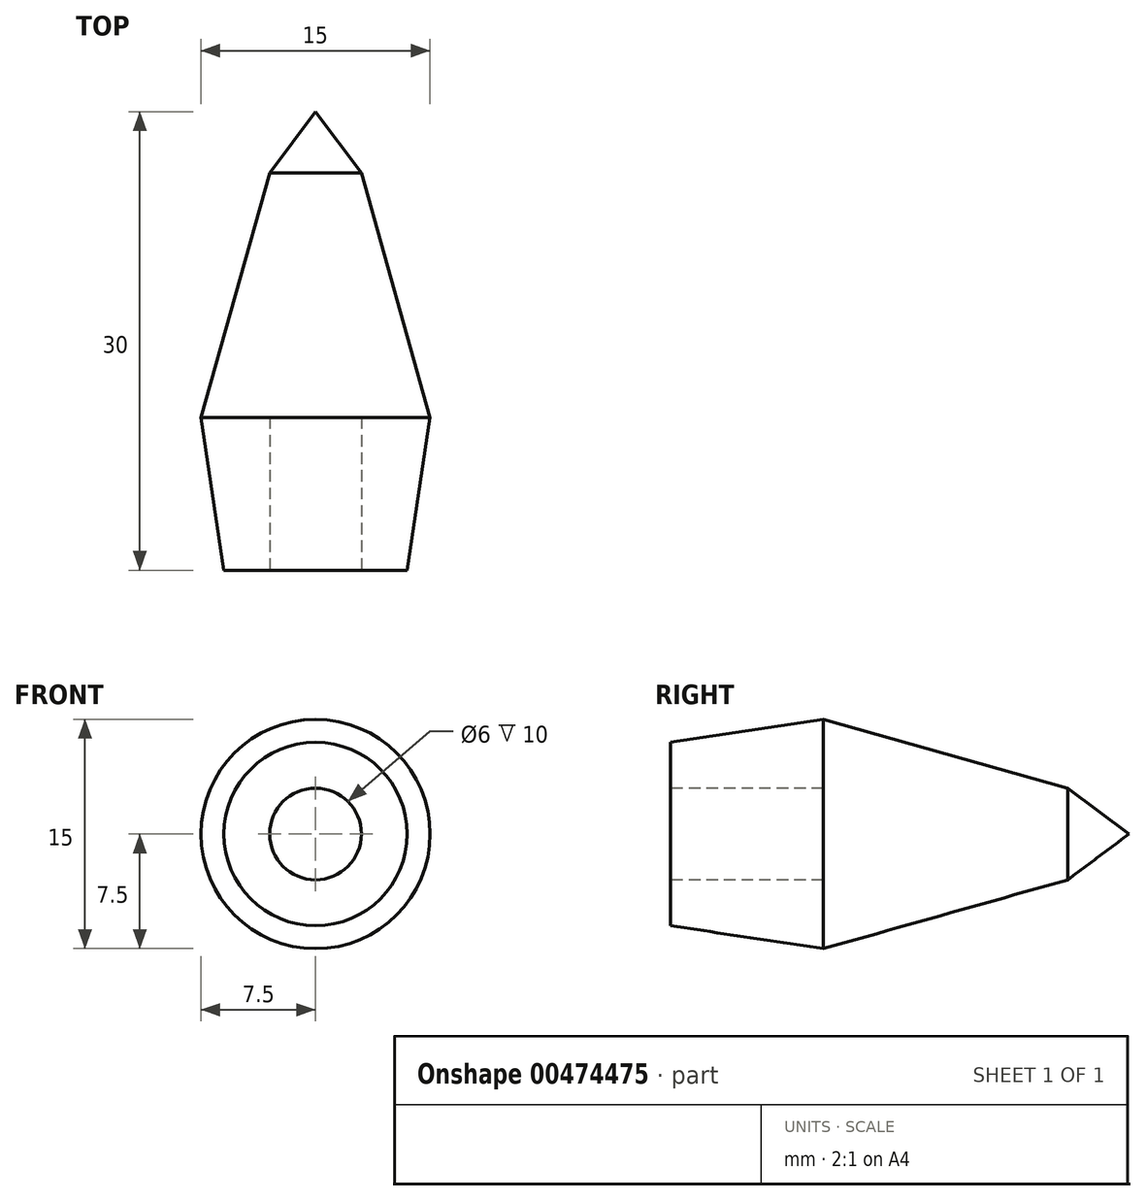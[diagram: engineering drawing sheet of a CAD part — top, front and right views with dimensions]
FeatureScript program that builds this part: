
annotation { "Feature Type Name" : "Feature", "Feature Type Description" : "" }
export const myFeature = defineFeature(function(context is Context, id is Id, definition is map)
    precondition{}
    {
        {
            var Q0;
            Q0=qCreatedBy(makeId("Right.planeOp"),FACE);
            var sketch = newSketch(context, id + "F0", { "sketchPlane" : qUnion([Q0])});
            skLineSegment(sketch, "E0", {"start": v(10.77, 0) * mm, "end": v(6.77, 3) * mm});
            skLineSegment(sketch, "E1", {"start": v(6.77, 3) * mm, "end": v(-9.23, 7.5) * mm});
            skLineSegment(sketch, "E2", {"start": v(-9.23, 7.5) * mm, "end": v(-19.23, 6) * mm});
            skPoint(sketch, "E3.orphan", {"position": v(-19.23, 0) * mm});
            skLineSegment(sketch, "E4", {"start": v(-31.66, 0) * mm, "end": v(29.62, 0) * mm, "construction": true});
            skLineSegment(sketch, "E5", {"start": v(-9.23, 0) * mm, "end": v(10.77, 0) * mm});
            skLineSegment(sketch, "E6", {"start": v(-19.23, 6) * mm, "end": v(-19.23, 3) * mm});
            skLineSegment(sketch, "E7", {"start": v(-19.23, 3) * mm, "end": v(-9.23, 3) * mm});
            skLineSegment(sketch, "E8", {"start": v(-9.23, 3) * mm, "end": v(-9.23, 0) * mm});
            skSolve(sketch);
        }
        {
            var Q0;
            Q0 = qSketchRegion(id + "F0", true);
            var Q1;
            Q1=sQuery(id+"F0.wireOp",EDGE,"E4");
            revolve(context, id + "F1", {"entities" : qUnion([Q0]), "axis" : qUnion([Q1]), "revolveType" : RevolveType.FULL});
        }
    });
